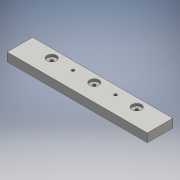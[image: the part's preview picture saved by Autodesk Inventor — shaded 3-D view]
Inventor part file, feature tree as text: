
AUTODESK INVENTOR PART (.ipt)
format: ipt  version: 2016 (Build 200138000, 138)  size: 117,760 bytes
history: native  units: mm
features: sketch x3, hole x2, extrude x1
ambient origin geometry x8: Origin, YZ Plane, XZ Plane, XY Plane, X Axis, Y Axis, Z Axis, Center Point
bodies: Solid1 (feature_tree)
feature tree (6):
  extrude  "Extrusion1"  Depth=30.0mm
  hole  "Hole1"  [1 undecoded]
  hole  "Hole2"  [1 undecoded]
  sketch  "Sketch1"  dims[d0=165.0mm d1=30.0mm]
  sketch  "Sketch2"  dims[d2=82.5mm d3=15.0mm]
  sketch  "Sketch3"  dims[d4=10.0mm d5=0.0mm d6=50.0mm d8=3.4mm d9=6.0mm d10=11.0mm d11=2.6mm d12=90.0deg d13=8.0mm d14=20.594885mm d15=50.0mm d17=3.242mm d18=8.0mm d19=12.6mm d20=2.0mm d21=90.0deg d22=11.8mm d23=20.594885mm d24=50.0mm d25=10.0mm d26=10.0mm d27=25.0mm d28=1.0mm d29=1.0mm]
note: 2 required parameter values undecoded (feature->parameter linkage not recoverable at this tier; creation-order binding heuristic only, values carry confidence <= 0.55)
